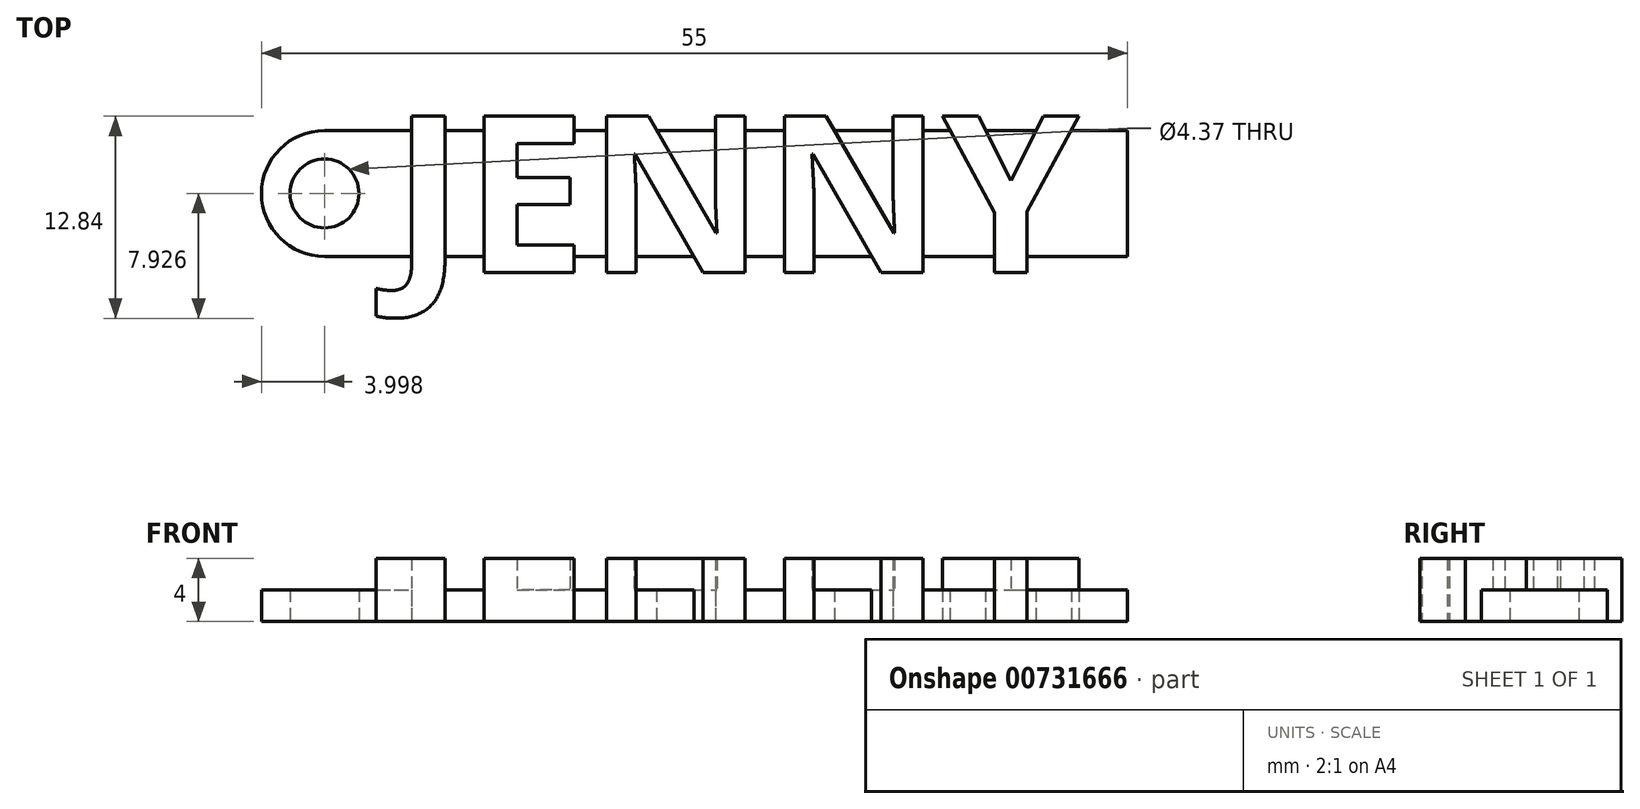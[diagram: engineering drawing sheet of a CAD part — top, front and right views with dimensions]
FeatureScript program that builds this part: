
annotation { "Feature Type Name" : "Feature", "Feature Type Description" : "" }
export const myFeature = defineFeature(function(context is Context, id is Id, definition is map)
    precondition{}
    {
        {
            var Q0;
            Q0=qCreatedBy(makeId("Top.planeOp"),FACE);
            var sketch = newSketch(context, id + "F0", { "sketchPlane" : qUnion([Q0])});
            skLineSegment(sketch, "E0.bottom", {"start": v(-14.78, 5.4) * mm, "end": v(41.05, 5.4) * mm});
            skLineSegment(sketch, "E0.top", {"start": v(-14.78, -2.6) * mm, "end": v(41.05, -2.6) * mm});
            skLineSegment(sketch, "E0.right", {"start": v(41.05, 5.4) * mm, "end": v(41.05, -2.6) * mm});
            skText(sketch, "E1", { "text": "JENNY", "fontName": "OpenSans-Bold.ttf"});
            skLineSegment(sketch, "E2", {"start": v(-9.95, 5.4) * mm, "end": v(-14.78, 5.4) * mm});
            skLineSegment(sketch, "E3", {"start": v(-9.95, 5.4) * mm, "end": v(-9.95, -2.6) * mm});
            skLineSegment(sketch, "E4", {"start": v(-14.78, -2.6) * mm, "end": v(-9.95, -2.6) * mm});
            skArc(sketch, "E5", {"start": v(-9.95, 5.4) * mm, "mid": v(-13.95, 1.4) * mm, "end": v(-9.95, -2.6) * mm});
            skCircle(sketch, "E6", {"center": v(-9.95, 1.4) * mm, "radius": 2.19 * mm});
            const initialGuessF0  = {"E1": [-0.00566, -0.0036, 1, 0, 0.01]};
            skSetInitialGuess(sketch, initialGuessF0);
            skSolve(sketch);
        }
        {
            var Q0;
            {var subQ0=sQuery(id+"F0.wireOp",EDGE,"E1.sketch_text.stroke-5");var subQ1=sQuery(id+"F0.wireOp",EDGE,"E0.bottom");var subQ2=makeQuery(id+"F0.imprint","INTERSECT",VERTEX,{"derivedFrom":[subQ1,subQ0]});Q0=makeQuery(id+"F0.imprint","IMPRINT",FACE,{"disambiguationData":[TD([[makeQuery(id+"F0.imprint","IMPRINT",EDGE,{"disambiguationData":[TD([[subQ2,-1.0]])],"derivedFrom":subQ1}),-1.0]])]});}
            var Q1;
            {var subQ5=sQuery(id+"F0.wireOp",EDGE,"E1.sketch_text.stroke-6");Q1=makeQuery(id+"F0.imprint","IMPRINT",FACE,{"disambiguationData":[TD([[makeQuery(id+"F0.imprint","IMPRINT",EDGE,{"derivedFrom":subQ5}),-1.0]])]});}
            var Q2;
            Q2=makeQuery(id+"F0.imprint","IMPRINT",FACE,{"disambiguationData":[TD([[makeQuery(id+"F0.imprint","IMPRINT",EDGE,{"derivedFrom":sQuery(id+"F0.wireOp",EDGE,"E1.sketch_text.stroke-0")}),-1.0]])]});
            var Q3;
            {var subQ5=sQuery(id+"F0.wireOp",EDGE,"E1.sketch_text.stroke-10");Q3=makeQuery(id+"F0.imprint","IMPRINT",FACE,{"disambiguationData":[TD([[makeQuery(id+"F0.imprint","IMPRINT",EDGE,{"derivedFrom":subQ5}),-1.0]])]});}
            var Q4;
            {var subQ0=sQuery(id+"F0.wireOp",EDGE,"E1.sketch_text.stroke-14");Q4=makeQuery(id+"F0.imprint","IMPRINT",FACE,{"disambiguationData":[TD([[makeQuery(id+"F0.imprint","IMPRINT",EDGE,{"derivedFrom":subQ0}),-1.0]])]});}
            var Q5;
            {var subQ5=sQuery(id+"F0.wireOp",EDGE,"E1.sketch_text.stroke-12");Q5=makeQuery(id+"F0.imprint","IMPRINT",FACE,{"disambiguationData":[TD([[makeQuery(id+"F0.imprint","IMPRINT",EDGE,{"derivedFrom":subQ5}),-1.0]])]});}
            var Q6;
            {var subQ5=sQuery(id+"F0.wireOp",EDGE,"E1.sketch_text.stroke-29");Q6=makeQuery(id+"F0.imprint","IMPRINT",FACE,{"disambiguationData":[TD([[makeQuery(id+"F0.imprint","IMPRINT",EDGE,{"derivedFrom":subQ5}),-1.0]])]});}
            var Q7;
            {var subQ13=sQuery(id+"F0.wireOp",EDGE,"E1.sketch_text.stroke-24");Q7=makeQuery(id+"F0.imprint","IMPRINT",FACE,{"disambiguationData":[TD([[makeQuery(id+"F0.imprint","IMPRINT",EDGE,{"derivedFrom":subQ13}),-1.0]])]});}
            var Q8;
            {var subQ5=sQuery(id+"F0.wireOp",EDGE,"E1.sketch_text.stroke-27");Q8=makeQuery(id+"F0.imprint","IMPRINT",FACE,{"disambiguationData":[TD([[makeQuery(id+"F0.imprint","IMPRINT",EDGE,{"derivedFrom":subQ5}),-1.0]])]});}
            var Q9;
            {var subQ5=sQuery(id+"F0.wireOp",EDGE,"E1.sketch_text.stroke-22");Q9=makeQuery(id+"F0.imprint","IMPRINT",FACE,{"disambiguationData":[TD([[makeQuery(id+"F0.imprint","IMPRINT",EDGE,{"derivedFrom":subQ5}),-1.0]])]});}
            var Q10;
            {var subQ5=sQuery(id+"F0.wireOp",EDGE,"E1.sketch_text.stroke-34");Q10=makeQuery(id+"F0.imprint","IMPRINT",FACE,{"disambiguationData":[TD([[makeQuery(id+"F0.imprint","IMPRINT",EDGE,{"derivedFrom":subQ5}),-1.0]])]});}
            var Q11;
            {var subQ5=sQuery(id+"F0.wireOp",EDGE,"E1.sketch_text.stroke-43");Q11=makeQuery(id+"F0.imprint","IMPRINT",FACE,{"disambiguationData":[TD([[makeQuery(id+"F0.imprint","IMPRINT",EDGE,{"derivedFrom":subQ5}),-1.0]])]});}
            var Q12;
            {var subQ8=sQuery(id+"F0.wireOp",EDGE,"E1.sketch_text.stroke-38");Q12=makeQuery(id+"F0.imprint","IMPRINT",FACE,{"disambiguationData":[TD([[makeQuery(id+"F0.imprint","IMPRINT",EDGE,{"derivedFrom":subQ8}),-1.0]])]});}
            var Q13;
            {var subQ5=sQuery(id+"F0.wireOp",EDGE,"E1.sketch_text.stroke-48");Q13=makeQuery(id+"F0.imprint","IMPRINT",FACE,{"disambiguationData":[TD([[makeQuery(id+"F0.imprint","IMPRINT",EDGE,{"derivedFrom":subQ5}),-1.0]])]});}
            var Q14;
            {var subQ5=sQuery(id+"F0.wireOp",EDGE,"E1.sketch_text.stroke-36");Q14=makeQuery(id+"F0.imprint","IMPRINT",FACE,{"disambiguationData":[TD([[makeQuery(id+"F0.imprint","IMPRINT",EDGE,{"derivedFrom":subQ5}),-1.0]])]});}
            var Q15;
            {var subQ5=sQuery(id+"F0.wireOp",EDGE,"E1.sketch_text.stroke-41");Q15=makeQuery(id+"F0.imprint","IMPRINT",FACE,{"disambiguationData":[TD([[makeQuery(id+"F0.imprint","IMPRINT",EDGE,{"derivedFrom":subQ5}),-1.0]])]});}
            var Q16;
            {var subQ5=sQuery(id+"F0.wireOp",EDGE,"E1.sketch_text.stroke-54");Q16=makeQuery(id+"F0.imprint","IMPRINT",FACE,{"disambiguationData":[TD([[makeQuery(id+"F0.imprint","IMPRINT",EDGE,{"derivedFrom":subQ5}),-1.0]])]});}
            var Q17;
            {var subQ3=sQuery(id+"F0.wireOp",EDGE,"E0.bottom");var subQ12=sQuery(id+"F0.wireOp",EDGE,"E1.sketch_text.stroke-56");var subQ13=makeQuery(id+"F0.imprint","INTERSECT",VERTEX,{"derivedFrom":[subQ3,subQ12]});Q17=makeQuery(id+"F0.imprint","IMPRINT",FACE,{"disambiguationData":[TD([[makeQuery(id+"F0.imprint","IMPRINT",EDGE,{"disambiguationData":[TD([[subQ13,-1.0]])],"derivedFrom":subQ3}),-1.0]])]});}
            var Q18;
            {var subQ5=sQuery(id+"F0.wireOp",EDGE,"E1.sketch_text.stroke-57");Q18=makeQuery(id+"F0.imprint","IMPRINT",FACE,{"disambiguationData":[TD([[makeQuery(id+"F0.imprint","IMPRINT",EDGE,{"derivedFrom":subQ5}),-1.0]])]});}
            var Q19;
            {var subQ5=sQuery(id+"F0.wireOp",EDGE,"E1.sketch_text.stroke-51");Q19=makeQuery(id+"F0.imprint","IMPRINT",FACE,{"disambiguationData":[TD([[makeQuery(id+"F0.imprint","IMPRINT",EDGE,{"derivedFrom":subQ5}),-1.0]])]});}
            extrude(context, id + "F1", {"entities" : qUnion([Q0, Q1, Q2, Q3, Q4, Q5, Q6, Q7, Q8, Q9, Q10, Q11, Q12, Q13, Q14, Q15, Q16, Q17, Q18, Q19]), "depth" : 4 * mm, "offsetDistance" : 25 * mm});
        }
        {
            var Q0;
            Q0 = qSketchRegion(id + "F0", true);
            extrude(context, id + "F2", {"entities" : qUnion([Q0]), "operationType" : NewBodyOperationType.ADD, "depth" : 2 * mm, "offsetDistance" : 25 * mm});
        }
    });
